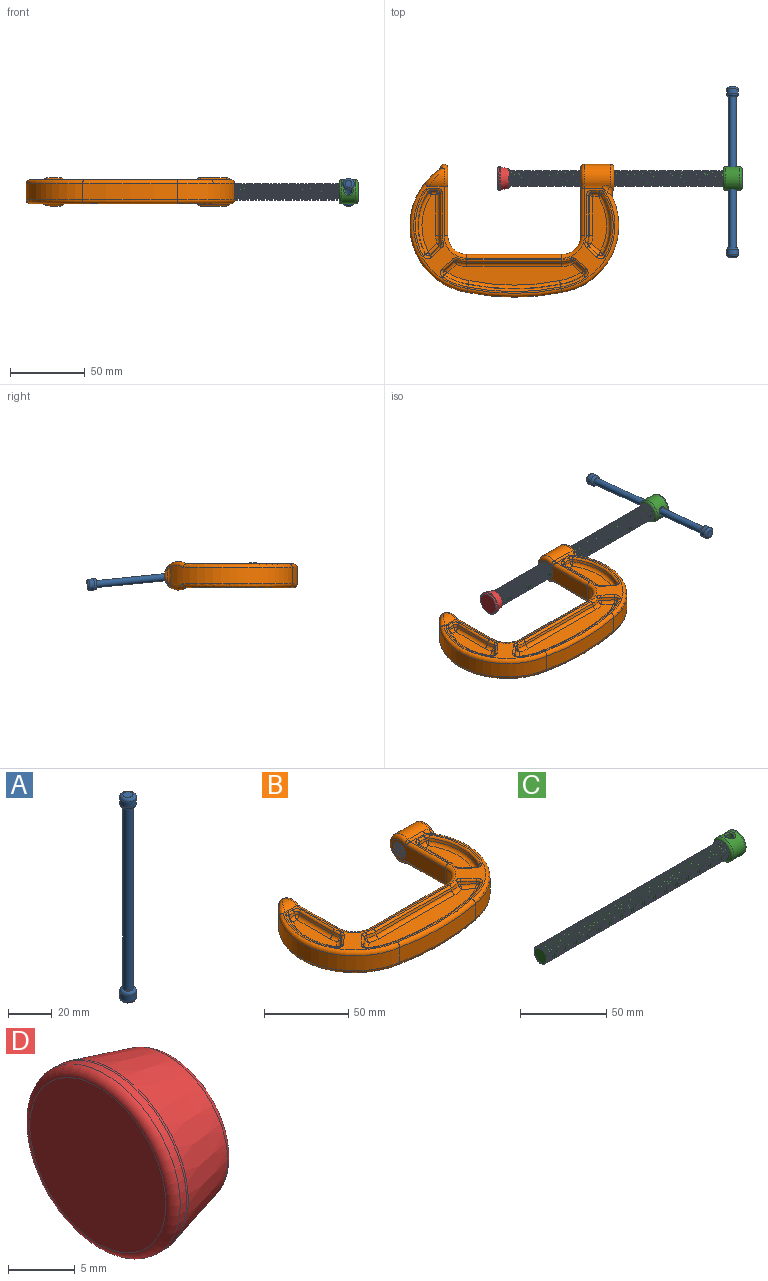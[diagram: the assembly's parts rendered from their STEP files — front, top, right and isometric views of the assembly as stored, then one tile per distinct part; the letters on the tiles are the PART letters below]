
ASSEMBLY  parts=4 mates=4
PART A: 11 faces, bbox 8.2x8.2x114.3 mm
  f0: cylinder r=2.37mm len=101.6mm, axis (0,0,-1), area 1516.1mm2, adj f1,f2
  f1: plane 4.75x4.75mm, normal (0,0,1), area 1.3mm2, adj f0,f9
  f2: plane 4.75x4.75mm, normal (0,0,-1), area 1.3mm2, adj f0,f5
  f3: cylinder r=3.81mm len=7.62mm, axis (0,0,1), area 79mm2, adj f5,f6
  f4: plane 4.57x4.57mm, normal (0,0,-1), area 16.4mm2, adj f6
  f5: torus R=2.29mm, axis (0,0,-1), area 49mm2, adj f2,f3
  f6: torus R=2.29mm, axis (0,0,-1), area 49mm2, adj f3,f4
  f7: cylinder r=3.81mm len=7.62mm, axis (0,0,-1), area 79mm2, adj f9,f10
  f8: plane 4.57x4.57mm, normal (0,0,1), area 16.4mm2, adj f10
  f9: torus R=2.29mm, axis (0,0,1), area 49mm2, adj f1,f7
  f10: torus R=2.29mm, axis (0,0,1), area 49mm2, adj f7,f8
PART B: 240 faces, bbox 147.4x103.1x20.9 mm
  f0: plane 45.3x14.18mm, normal (-1,0,0), area 415mm2, adj f8,f12,f13,f128,f236,f237,f238,f239
  f1: plane 14.21x14.21mm, normal (1,0,0), area 70.7mm2, adj f23,f24,f236,f237,f238,f239
  f2: cylinder r=9.53mm len=11.89mm, axis (1,0,0), area 65.6mm2, adj f10,f18,f19
  f3: cylinder r=45.26mm len=82.03mm, axis (0,0,-1), area 1160.1mm2, adj f6,f19,f20,f32,f133,f134
  f4: cylinder r=12.7mm len=12.7mm, axis (0,0,-1), area 215.4mm2, adj f5,f9,f16,f131
  f5: plane 45.09x13.97mm, normal (1,0,0), area 497.5mm2, adj f4,f17,f18,f132
  f6: cylinder r=160.34mm len=63.5mm, axis (0,0,-1), area 690mm2, adj f3,f7,f22,f136
  f7: cylinder r=45.26mm len=63.81mm, axis (0,0,-1), area 898.1mm2, adj f6,f21,f29,f30,f135,f141
  f8: cylinder r=12.7mm len=12.7mm, axis (0,0,-1), area 215.4mm2, adj f0,f9,f14,f129
  f9: plane 63.5x10.8mm, normal (0,1,0), area 685.5mm2, adj f4,f8,f15,f130
  f10: plane 134.76x72.01mm, normal (0,0,1), area 839.3mm2, adj f2,f13,f14,f15,f16,f17,f19,f20
  f11: cylinder r=9.53mm len=19.05mm, axis (-1,0,0), area 671.5mm2, adj f12,f23,f26,f27,f138,f139
  f12: torus R=6.99mm, axis (-1,0,0), area 147.2mm2, adj f0,f11,f25,f137
  f13: cylinder r=2.54mm len=33.67mm, axis (0,1,0), area 130mm2, adj f0,f10,f14,f25
  f14: torus R=15.24mm, axis (0,0,1), area 85.4mm2, adj f8,f10,f13,f15
  f15: cylinder r=2.54mm len=63.5mm, axis (1,0,0), area 253.4mm2, adj f9,f10,f14,f16
  f16: torus R=15.24mm, axis (0,0,1), area 85.4mm2, adj f4,f10,f15,f17
  f17: cylinder r=2.54mm len=33.67mm, axis (0,-1,0), area 132.7mm2, adj f5,f10,f16,f18
  f18: torus R=6.99mm, axis (-1,0,0), area 185.7mm2, adj f2,f5,f17,f31,f32,f126,f132,f142
  f19: bspline ~14.84x14.22mm, area 58.9mm2, adj f2,f3,f10,f20,f31
  f20: torus R=42.72mm, axis (0,0,1), area 369.9mm2, adj f3,f10,f19,f22
  f21: torus R=42.72mm, axis (0,0,1), area 340.5mm2, adj f7,f10,f22,f27,f28
  f22: torus R=157.8mm, axis (0,0,1), area 253.8mm2, adj f6,f10,f20,f21
  f23: torus R=6.99mm, axis (-1,0,0), area 177.3mm2, adj f1,f11,f24,f28,f29,f140,f141
  f24: bspline ~4.38x2.8mm, area 1.6mm2, adj f1,f23,f30
  f25: bspline ~3.1x3.02mm, area 4mm2, adj f12,f13,f26
  f26: cylinder r=5.08mm len=12.32mm, axis (-1,0,0), area 29.4mm2, adj f10,f11,f25,f27
  f27: bspline ~6.24x5.06mm, area 14.2mm2, adj f11,f21,f26,f28
  f28: bspline ~8.05x5.04mm, area 22.7mm2, adj f21,f23,f27,f29
  f29: bspline ~10x6.13mm, area 20.5mm2, adj f7,f23,f28,f30
  f30: bspline ~4.94x4.9mm, area 7mm2, adj f7,f24,f29,f141
  f31: bspline ~3.25x2.6mm, area 2.6mm2, adj f18,f19,f32
  f32: bspline ~12.33x2.68mm, area 31.2mm2, adj f3,f18,f31,f142
  f33: cone r=2.54mm half-angle=15deg, axis (0,0,1), area 4mm2, adj f34,f41,f74,f100
  f34: cone r=17.53mm half-angle=15deg, axis (0,0,-1), area 9.3mm2, adj f33,f35,f73,f102
  f35: plane 28.01x1.74mm, normal (-0.97,0,0.26), area 50.4mm2, adj f34,f36,f71,f104
  f36: cone r=2.54mm half-angle=15deg, axis (0,0,1), area 5.7mm2, adj f35,f37,f69,f103
  f37: plane 4.03x1.74mm, normal (0,-0.97,0.26), area 7.3mm2, adj f36,f38,f67,f101
  f38: cone r=2.54mm half-angle=15deg, axis (0,0,1), area 3.5mm2, adj f37,f39,f66,f99
  f39: cone r=40.43mm half-angle=15deg, axis (0,0,1), area 79.5mm2, adj f38,f40,f68,f97
  f40: cone r=2.54mm half-angle=15deg, axis (0,0,1), area 6.5mm2, adj f39,f41,f70,f96
  f41: plane 7.02x6.52mm, normal (-0.65,0.71,0.26), area 16.4mm2, adj f33,f40,f72,f98
  f42: plane 38.05x10.03mm, normal (0,0,1), area 277.8mm2, adj f67,f68,f71,f72,f73
  f43: plane 7.02x6.52mm, normal (0.65,-0.71,0.26), area 16.4mm2, adj f44,f54,f83,f123
  f44: cone r=2.54mm half-angle=15deg, axis (0,0,1), area 6.5mm2, adj f43,f45,f81,f125
  f45: cone r=40.43mm half-angle=15deg, axis (0,0,1), area 31.1mm2, adj f44,f46,f79,f124
  f46: cone r=155.51mm half-angle=15deg, axis (0,0,1), area 111.5mm2, adj f45,f47,f77,f122
  f47: cone r=40.43mm half-angle=15deg, axis (0,0,1), area 31.1mm2, adj f46,f48,f75,f120
  f48: cone r=2.54mm half-angle=15deg, axis (0,0,1), area 6.5mm2, adj f47,f49,f76,f118
  f49: plane 7.02x6.52mm, normal (-0.65,-0.71,0.26), area 16.4mm2, adj f48,f50,f78,f116
  f50: cone r=2.54mm half-angle=15deg, axis (0,0,1), area 4mm2, adj f49,f51,f80,f114
  f51: cone r=17.53mm half-angle=15deg, axis (0,0,-1), area 12mm2, adj f50,f52,f82,f115
  f52: plane 63.5x1.74mm, normal (0,-0.97,0.26), area 114.2mm2, adj f51,f53,f84,f117
  f53: cone r=17.53mm half-angle=15deg, axis (0,0,-1), area 12mm2, adj f52,f54,f86,f119
  f54: cone r=2.54mm half-angle=15deg, axis (0,0,1), area 4mm2, adj f43,f53,f85,f121
  f55: plane 89.13x13.72mm, normal (0,0,1), area 893.1mm2, adj f75,f77,f78,f79,f82,f83,f84,f86
  f56: plane 4.92x1.74mm, normal (0,-0.97,0.26), area 8.8mm2, adj f57,f64,f93,f110
  f57: cone r=2.54mm half-angle=15deg, axis (0,0,1), area 5.7mm2, adj f56,f58,f95,f108
  f58: plane 26.65x1.74mm, normal (0.97,0,0.26), area 47.9mm2, adj f57,f59,f94,f106
  f59: cone r=17.53mm half-angle=15deg, axis (0,0,-1), area 9.3mm2, adj f58,f60,f92,f105
  f60: cone r=2.54mm half-angle=15deg, axis (0,0,1), area 4mm2, adj f59,f61,f90,f107
  f61: plane 7.02x6.52mm, normal (0.65,0.71,0.26), area 16.4mm2, adj f60,f62,f88,f109
  f62: cone r=2.54mm half-angle=15deg, axis (0,0,1), area 6.5mm2, adj f61,f63,f87,f111
  f63: cone r=40.43mm half-angle=15deg, axis (0,0,1), area 76.5mm2, adj f62,f64,f89,f113
  f64: cone r=2.54mm half-angle=15deg, axis (0,0,1), area 3.7mm2, adj f56,f63,f91,f112
  f65: plane 36.69x10.03mm, normal (0,0,1), area 273.1mm2, adj f88,f89,f92,f93,f94
  f66: bspline ~2.45x1.88mm, area 2.1mm2, adj f38,f67,f68
  f67: cylinder r=2.54mm len=4.03mm, axis (-1,0,0), area 11.7mm2, adj f37,f42,f66,f69
  f68: torus R=37.21mm, axis (0,0,1), area 140.3mm2, adj f39,f42,f66,f70
  f69: bspline ~2.45x2.45mm, area 3.4mm2, adj f36,f67,f71
  f70: bspline ~2.8x2.75mm, area 3.9mm2, adj f40,f68,f72
  f71: cylinder r=2.54mm len=28.01mm, axis (0,1,0), area 92mm2, adj f35,f42,f69,f73
  f72: cylinder r=2.54mm len=8.37mm, axis (-0.74,-0.68,0), area 28.2mm2, adj f41,f42,f70,f74
  f73: torus R=20.75mm, axis (0,0,1), area 17.6mm2, adj f34,f42,f71,f74
  f74: bspline ~2.53x1.88mm, area 2.4mm2, adj f33,f72,f73
  f75: torus R=37.21mm, axis (0,0,1), area 54.4mm2, adj f47,f55,f76,f77
  f76: bspline ~2.81x2.78mm, area 3.9mm2, adj f48,f75,f78
  f77: torus R=152.29mm, axis (0,0,1), area 204.7mm2, adj f46,f55,f75,f79
  f78: cylinder r=2.54mm len=8.37mm, axis (0.74,-0.68,0), area 28.2mm2, adj f49,f55,f76,f80
  f79: torus R=37.21mm, axis (0,0,1), area 54.4mm2, adj f45,f55,f77,f81
  f80: bspline ~2.55x1.88mm, area 2.4mm2, adj f50,f78,f82
  f81: bspline ~2.81x2.78mm, area 3.9mm2, adj f44,f79,f83
  f82: torus R=20.75mm, axis (0,0,1), area 22.9mm2, adj f51,f55,f80,f84
  f83: cylinder r=2.54mm len=8.37mm, axis (-0.74,-0.68,0), area 28.2mm2, adj f43,f55,f81,f85
  f84: cylinder r=2.54mm len=63.5mm, axis (-1,0,0), area 211.1mm2, adj f52,f55,f82,f86
  f85: bspline ~2.55x1.88mm, area 2.4mm2, adj f54,f83,f86
  f86: torus R=20.75mm, axis (0,0,1), area 22.9mm2, adj f53,f55,f84,f85
  f87: bspline ~2.8x2.75mm, area 3.9mm2, adj f62,f88,f89
  f88: cylinder r=2.54mm len=8.37mm, axis (0.74,-0.68,0), area 28.2mm2, adj f61,f65,f87,f90
  f89: torus R=37.21mm, axis (0,0,1), area 134.8mm2, adj f63,f65,f87,f91
  f90: bspline ~2.53x1.88mm, area 2.4mm2, adj f60,f88,f92
  f91: bspline ~2.45x1.88mm, area 2.2mm2, adj f64,f89,f93
  f92: torus R=20.75mm, axis (0,0,1), area 17.6mm2, adj f59,f65,f90,f94
  f93: cylinder r=2.54mm len=4.92mm, axis (-1,0,0), area 14.6mm2, adj f56,f65,f91,f95
  f94: cylinder r=2.54mm len=26.65mm, axis (0,-1,0), area 87.5mm2, adj f58,f65,f92,f95
  f95: bspline ~2.45x2.45mm, area 3.4mm2, adj f57,f93,f94
  f96: torus R=3.71mm, axis (0,0,1), area 10.3mm2, adj f10,f40,f97,f98
  f97: torus R=41.6mm, axis (0,0,1), area 90mm2, adj f10,f39,f96,f99
  f98: cylinder r=1.52mm len=7.71mm, axis (0.74,0.68,0), area 18.2mm2, adj f10,f41,f96,f100
  f99: torus R=3.71mm, axis (0,0,1), area 5.5mm2, adj f10,f38,f97,f101
  f100: torus R=3.71mm, axis (0,0,1), area 6.3mm2, adj f10,f33,f98,f102
  f101: cylinder r=1.52mm len=4.03mm, axis (1,0,0), area 8mm2, adj f10,f37,f99,f103
  f102: torus R=16.36mm, axis (0,0,1), area 9.8mm2, adj f10,f34,f100,f104
  f103: torus R=3.71mm, axis (0,0,1), area 8.9mm2, adj f10,f36,f101,f104
  f104: cylinder r=1.52mm len=28.01mm, axis (0,-1,0), area 55.9mm2, adj f10,f35,f102,f103
  f105: torus R=16.36mm, axis (0,0,1), area 9.8mm2, adj f10,f59,f106,f107
  f106: cylinder r=1.52mm len=26.65mm, axis (0,1,0), area 53.2mm2, adj f10,f58,f105,f108
  f107: torus R=3.71mm, axis (0,0,1), area 6.3mm2, adj f10,f60,f105,f109
  f108: torus R=3.71mm, axis (0,0,1), area 8.9mm2, adj f10,f57,f106,f110
  f109: cylinder r=1.52mm len=7.71mm, axis (-0.74,0.68,0), area 18.2mm2, adj f10,f61,f107,f111
  f110: cylinder r=1.52mm len=4.92mm, axis (1,0,0), area 9.8mm2, adj f10,f56,f108,f112
  f111: torus R=3.71mm, axis (0,0,1), area 10.3mm2, adj f10,f62,f109,f113
  f112: torus R=3.71mm, axis (0,0,1), area 5.8mm2, adj f10,f64,f110,f113
  f113: torus R=41.6mm, axis (0,0,1), area 86.6mm2, adj f10,f63,f111,f112
  f114: torus R=3.71mm, axis (0,0,1), area 6.3mm2, adj f10,f50,f115,f116
  f115: torus R=16.36mm, axis (0,0,1), area 12.6mm2, adj f10,f51,f114,f117
  f116: cylinder r=1.52mm len=7.71mm, axis (-0.74,0.68,0), area 18.2mm2, adj f10,f49,f114,f118
  f117: cylinder r=1.52mm len=63.5mm, axis (1,0,0), area 126.7mm2, adj f10,f52,f115,f119
  f118: torus R=3.71mm, axis (0,0,1), area 10.3mm2, adj f10,f48,f116,f120
  f119: torus R=16.36mm, axis (0,0,1), area 12.6mm2, adj f10,f53,f117,f121
  f120: torus R=41.6mm, axis (0,0,1), area 35.2mm2, adj f10,f47,f118,f122
  f121: torus R=3.71mm, axis (0,0,1), area 6.3mm2, adj f10,f54,f119,f123
  f122: torus R=156.68mm, axis (0,0,1), area 124.3mm2, adj f10,f46,f120,f124
  f123: cylinder r=1.52mm len=7.71mm, axis (0.74,0.68,0), area 18.2mm2, adj f10,f43,f121,f125
  f124: torus R=41.6mm, axis (0,0,1), area 35.2mm2, adj f10,f45,f122,f125
  f125: torus R=3.71mm, axis (0,0,1), area 10.3mm2, adj f10,f44,f123,f124
  f126: cylinder r=9.53mm len=11.89mm, axis (1,0,0), area 65.6mm2, adj f18,f127,f133
  f127: plane 134.76x72.01mm, normal (0,0,-1), area 839.3mm2, adj f126,f128,f129,f130,f131,f132,f133,f134
  f128: cylinder r=2.54mm len=33.67mm, axis (0,1,0), area 130mm2, adj f0,f127,f129,f137
  f129: torus R=15.24mm, axis (0,0,-1), area 85.4mm2, adj f8,f127,f128,f130
  f130: cylinder r=2.54mm len=63.5mm, axis (1,0,0), area 253.4mm2, adj f9,f127,f129,f131
  f131: torus R=15.24mm, axis (0,0,-1), area 85.4mm2, adj f4,f127,f130,f132
  f132: cylinder r=2.54mm len=33.67mm, axis (0,-1,0), area 132.7mm2, adj f5,f18,f127,f131
  f133: bspline ~14.84x14.22mm, area 58.9mm2, adj f3,f126,f127,f134,f142
  f134: torus R=42.72mm, axis (0,0,-1), area 369.9mm2, adj f3,f127,f133,f136
  f135: torus R=42.72mm, axis (0,0,-1), area 340.5mm2, adj f7,f127,f136,f139,f140
  f136: torus R=157.8mm, axis (0,0,-1), area 253.8mm2, adj f6,f127,f134,f135
  f137: bspline ~3.1x3.02mm, area 4mm2, adj f12,f128,f138
  f138: cylinder r=5.08mm len=12.32mm, axis (-1,0,0), area 29.4mm2, adj f11,f127,f137,f139
  f139: bspline ~6.24x5.06mm, area 14.2mm2, adj f11,f135,f138,f140
  f140: bspline ~8.05x5.04mm, area 22.7mm2, adj f23,f135,f139,f141
  f141: bspline ~8.1x6.12mm, area 20.5mm2, adj f7,f23,f30,f140
  f142: bspline ~3.17x2.51mm, area 2.6mm2, adj f18,f32,f133
  f143: cone r=2.54mm half-angle=15deg, axis (0,0,-1), area 4mm2, adj f144,f151,f184,f210
  f144: cone r=17.53mm half-angle=15deg, axis (0,0,1), area 9.3mm2, adj f143,f145,f183,f212
  f145: plane 28.01x1.74mm, normal (-0.97,0,-0.26), area 50.4mm2, adj f144,f146,f181,f214
  f146: cone r=2.54mm half-angle=15deg, axis (0,0,-1), area 5.7mm2, adj f145,f147,f179,f213
  f147: plane 4.03x1.74mm, normal (0,-0.97,-0.26), area 7.3mm2, adj f146,f148,f177,f211
  f148: cone r=2.54mm half-angle=15deg, axis (0,0,-1), area 3.5mm2, adj f147,f149,f176,f209
  f149: cone r=40.43mm half-angle=15deg, axis (0,0,-1), area 79.5mm2, adj f148,f150,f178,f207
  f150: cone r=2.54mm half-angle=15deg, axis (0,0,-1), area 6.5mm2, adj f149,f151,f180,f206
  f151: plane 7.02x6.52mm, normal (-0.65,0.71,-0.26), area 16.4mm2, adj f143,f150,f182,f208
  f152: plane 38.05x10.03mm, normal (0,0,-1), area 277.8mm2, adj f177,f178,f181,f182,f183
  f153: plane 7.02x6.52mm, normal (0.65,-0.71,-0.26), area 16.4mm2, adj f154,f164,f193,f233
  f154: cone r=2.54mm half-angle=15deg, axis (0,0,-1), area 6.5mm2, adj f153,f155,f191,f235
  f155: cone r=40.43mm half-angle=15deg, axis (0,0,-1), area 31.1mm2, adj f154,f156,f189,f234
  f156: cone r=155.51mm half-angle=15deg, axis (0,0,-1), area 111.5mm2, adj f155,f157,f187,f232
  f157: cone r=40.43mm half-angle=15deg, axis (0,0,-1), area 31.1mm2, adj f156,f158,f185,f230
  f158: cone r=2.54mm half-angle=15deg, axis (0,0,-1), area 6.5mm2, adj f157,f159,f186,f228
  f159: plane 7.02x6.52mm, normal (-0.65,-0.71,-0.26), area 16.4mm2, adj f158,f160,f188,f226
  f160: cone r=2.54mm half-angle=15deg, axis (0,0,-1), area 4mm2, adj f159,f161,f190,f224
  f161: cone r=17.53mm half-angle=15deg, axis (0,0,1), area 12mm2, adj f160,f162,f192,f225
  f162: plane 63.5x1.74mm, normal (0,-0.97,-0.26), area 114.2mm2, adj f161,f163,f194,f227
  f163: cone r=17.53mm half-angle=15deg, axis (0,0,1), area 12mm2, adj f162,f164,f196,f229
  f164: cone r=2.54mm half-angle=15deg, axis (0,0,-1), area 4mm2, adj f153,f163,f195,f231
  f165: plane 89.13x13.72mm, normal (0,0,-1), area 893.1mm2, adj f185,f187,f188,f189,f192,f193,f194,f196
  f166: plane 4.92x1.74mm, normal (0,-0.97,-0.26), area 8.8mm2, adj f167,f174,f203,f220
  f167: cone r=2.54mm half-angle=15deg, axis (0,0,-1), area 5.7mm2, adj f166,f168,f205,f218
  f168: plane 26.65x1.74mm, normal (0.97,0,-0.26), area 47.9mm2, adj f167,f169,f204,f216
  f169: cone r=17.53mm half-angle=15deg, axis (0,0,1), area 9.3mm2, adj f168,f170,f202,f215
  f170: cone r=2.54mm half-angle=15deg, axis (0,0,-1), area 4mm2, adj f169,f171,f200,f217
  f171: plane 7.02x6.52mm, normal (0.65,0.71,-0.26), area 16.4mm2, adj f170,f172,f198,f219
  f172: cone r=2.54mm half-angle=15deg, axis (0,0,-1), area 6.5mm2, adj f171,f173,f197,f221
  f173: cone r=40.43mm half-angle=15deg, axis (0,0,-1), area 76.5mm2, adj f172,f174,f199,f223
  f174: cone r=2.54mm half-angle=15deg, axis (0,0,-1), area 3.7mm2, adj f166,f173,f201,f222
  f175: plane 36.69x10.03mm, normal (0,0,-1), area 273.1mm2, adj f198,f199,f202,f203,f204
  f176: bspline ~2.45x1.88mm, area 2.1mm2, adj f148,f177,f178
  f177: cylinder r=2.54mm len=4.03mm, axis (-1,0,0), area 11.7mm2, adj f147,f152,f176,f179
  f178: torus R=37.21mm, axis (0,0,-1), area 140.3mm2, adj f149,f152,f176,f180
  f179: bspline ~2.45x2.45mm, area 3.4mm2, adj f146,f177,f181
  f180: bspline ~2.8x2.75mm, area 3.9mm2, adj f150,f178,f182
  f181: cylinder r=2.54mm len=28.01mm, axis (0,1,0), area 92mm2, adj f145,f152,f179,f183
  f182: cylinder r=2.54mm len=8.37mm, axis (-0.74,-0.68,0), area 28.2mm2, adj f151,f152,f180,f184
  f183: torus R=20.75mm, axis (0,0,-1), area 17.6mm2, adj f144,f152,f181,f184
  f184: bspline ~2.53x1.88mm, area 2.4mm2, adj f143,f182,f183
  f185: torus R=37.21mm, axis (0,0,-1), area 54.4mm2, adj f157,f165,f186,f187
  f186: bspline ~2.81x2.78mm, area 3.9mm2, adj f158,f185,f188
  f187: torus R=152.29mm, axis (0,0,-1), area 204.7mm2, adj f156,f165,f185,f189
  f188: cylinder r=2.54mm len=8.37mm, axis (0.74,-0.68,0), area 28.2mm2, adj f159,f165,f186,f190
  f189: torus R=37.21mm, axis (0,0,-1), area 54.4mm2, adj f155,f165,f187,f191
  f190: bspline ~2.55x1.88mm, area 2.4mm2, adj f160,f188,f192
  f191: bspline ~2.81x2.78mm, area 3.9mm2, adj f154,f189,f193
  f192: torus R=20.75mm, axis (0,0,-1), area 22.9mm2, adj f161,f165,f190,f194
  f193: cylinder r=2.54mm len=8.37mm, axis (-0.74,-0.68,0), area 28.2mm2, adj f153,f165,f191,f195
  f194: cylinder r=2.54mm len=63.5mm, axis (-1,0,0), area 211.1mm2, adj f162,f165,f192,f196
  f195: bspline ~2.55x1.88mm, area 2.4mm2, adj f164,f193,f196
  f196: torus R=20.75mm, axis (0,0,-1), area 22.9mm2, adj f163,f165,f194,f195
  f197: bspline ~2.8x2.75mm, area 3.9mm2, adj f172,f198,f199
  f198: cylinder r=2.54mm len=8.37mm, axis (0.74,-0.68,0), area 28.2mm2, adj f171,f175,f197,f200
  f199: torus R=37.21mm, axis (0,0,-1), area 134.8mm2, adj f173,f175,f197,f201
  f200: bspline ~2.53x1.88mm, area 2.4mm2, adj f170,f198,f202
  f201: bspline ~2.45x1.88mm, area 2.2mm2, adj f174,f199,f203
  f202: torus R=20.75mm, axis (0,0,-1), area 17.6mm2, adj f169,f175,f200,f204
  f203: cylinder r=2.54mm len=4.92mm, axis (-1,0,0), area 14.6mm2, adj f166,f175,f201,f205
  f204: cylinder r=2.54mm len=26.65mm, axis (0,-1,0), area 87.5mm2, adj f168,f175,f202,f205
  f205: bspline ~2.45x2.45mm, area 3.4mm2, adj f167,f203,f204
  f206: torus R=3.71mm, axis (0,0,-1), area 10.3mm2, adj f127,f150,f207,f208
  f207: torus R=41.6mm, axis (0,0,-1), area 90mm2, adj f127,f149,f206,f209
  f208: cylinder r=1.52mm len=7.71mm, axis (0.74,0.68,0), area 18.2mm2, adj f127,f151,f206,f210
  f209: torus R=3.71mm, axis (0,0,-1), area 5.5mm2, adj f127,f148,f207,f211
  f210: torus R=3.71mm, axis (0,0,-1), area 6.3mm2, adj f127,f143,f208,f212
  f211: cylinder r=1.52mm len=4.03mm, axis (1,0,0), area 8mm2, adj f127,f147,f209,f213
  f212: torus R=16.36mm, axis (0,0,-1), area 9.8mm2, adj f127,f144,f210,f214
  f213: torus R=3.71mm, axis (0,0,-1), area 8.9mm2, adj f127,f146,f211,f214
  f214: cylinder r=1.52mm len=28.01mm, axis (0,-1,0), area 55.9mm2, adj f127,f145,f212,f213
  f215: torus R=16.36mm, axis (0,0,-1), area 9.8mm2, adj f127,f169,f216,f217
  f216: cylinder r=1.52mm len=26.65mm, axis (0,1,0), area 53.2mm2, adj f127,f168,f215,f218
  f217: torus R=3.71mm, axis (0,0,-1), area 6.3mm2, adj f127,f170,f215,f219
  f218: torus R=3.71mm, axis (0,0,-1), area 8.9mm2, adj f127,f167,f216,f220
  f219: cylinder r=1.52mm len=7.71mm, axis (-0.74,0.68,0), area 18.2mm2, adj f127,f171,f217,f221
  f220: cylinder r=1.52mm len=4.92mm, axis (1,0,0), area 9.8mm2, adj f127,f166,f218,f222
  f221: torus R=3.71mm, axis (0,0,-1), area 10.3mm2, adj f127,f172,f219,f223
  f222: torus R=3.71mm, axis (0,0,-1), area 5.8mm2, adj f127,f174,f220,f223
  f223: torus R=41.6mm, axis (0,0,-1), area 86.6mm2, adj f127,f173,f221,f222
  f224: torus R=3.71mm, axis (0,0,-1), area 6.3mm2, adj f127,f160,f225,f226
  f225: torus R=16.36mm, axis (0,0,-1), area 12.6mm2, adj f127,f161,f224,f227
  f226: cylinder r=1.52mm len=7.71mm, axis (-0.74,0.68,0), area 18.2mm2, adj f127,f159,f224,f228
  f227: cylinder r=1.52mm len=63.5mm, axis (1,0,0), area 126.7mm2, adj f127,f162,f225,f229
  f228: torus R=3.71mm, axis (0,0,-1), area 10.3mm2, adj f127,f158,f226,f230
  f229: torus R=16.36mm, axis (0,0,-1), area 12.6mm2, adj f127,f163,f227,f231
  f230: torus R=41.6mm, axis (0,0,-1), area 35.2mm2, adj f127,f157,f228,f232
  f231: torus R=3.71mm, axis (0,0,-1), area 6.3mm2, adj f127,f164,f229,f233
  f232: torus R=156.68mm, axis (0,0,-1), area 124.3mm2, adj f127,f156,f230,f234
  f233: cylinder r=1.52mm len=7.71mm, axis (0.74,0.68,0), area 18.2mm2, adj f127,f153,f231,f235
  f234: torus R=41.6mm, axis (0,0,-1), area 35.2mm2, adj f127,f155,f232,f235
  f235: torus R=3.71mm, axis (0,0,-1), area 10.3mm2, adj f127,f154,f233,f234
  f236: cylinder r=5.56mm len=22.23mm, axis (-1,0,0), area 259.9mm2, adj f0,f1,f237,f238
  f237: bspline ~22.77x12.85mm, area 365.3mm2, adj f0,f1,f236,f239
  f238: bspline ~23.07x12.85mm, area 365.3mm2, adj f0,f1,f236,f239
  f239: cylinder r=4.67mm len=22.23mm, axis (-1,0,0), area 225.7mm2, adj f0,f1,f237,f238
PART C: 13 faces, bbox 162.5x17.4x17.4 mm
  f0: plane 13.07x13.07mm, normal (-1,0,0), area 46.6mm2, adj f3,f4,f5,f6,f9
  f1: cylinder r=7.94mm len=15.88mm, axis (1,0,0), area 411.2mm2, adj f8,f9,f11,f12
  f2: plane 10.67x10.46mm, normal (-1,0,0), area 82.6mm2, adj f3,f4,f5,f6
  f3: cylinder r=5.56mm len=149.23mm, axis (-1,0,0), area -309mm2, adj f0,f2,f4,f5
  f4: bspline ~149.91x12.85mm, area 2458.9mm2, adj f0,f2,f3,f6
  f5: bspline ~149.91x12.85mm, area 2458.1mm2, adj f0,f2,f3,f6
  f6: cylinder r=4.67mm len=149.23mm, axis (-1,0,0), area -750.6mm2, adj f0,f2,f4,f5
  f7: plane 12.83x12.83mm, normal (1,0,0), area 129.2mm2, adj f8
  f8: torus R=6.41mm, axis (1,0,0), area 111.1mm2, adj f1,f7
  f9: torus R=6.41mm, axis (1,0,0), area 111.1mm2, adj f0,f1
  f10: cylinder r=2.37mm len=14.35mm, axis (0,0,1), area 203.5mm2, adj f11,f12
  f11: bspline ~6.95x6.28mm, area 23.6mm2, adj f1,f10
  f12: bspline ~6.95x6.28mm, area 23.6mm2, adj f1,f10
PART D: 12 faces, bbox 8.6x17.4x17.4 mm
  f0: plane 11.56x11.56mm, normal (1,0,0), area 17.7mm2, adj f6,f7,f8,f9,f10
  f1: cone r=7.94mm half-angle=15deg, axis (-1,0,0), area 264.5mm2, adj f4,f6
  f2: plane 14.35x14.35mm, normal (-1,0,0), area 161.8mm2, adj f5
  f3: cylinder r=7.94mm len=15.88mm, axis (-1,0,0), area 33mm2, adj f4,f5
  f4: torus R=7.18mm, axis (1,0,0), area 9.9mm2, adj f1,f3
  f5: torus R=7.18mm, axis (-1,0,0), area 57.6mm2, adj f2,f3
  f6: torus R=5.65mm, axis (-1,0,0), area 38.1mm2, adj f0,f1
  f7: cylinder r=5.56mm len=11.13mm, axis (-1,0,0), area 80.5mm2, adj f0,f8,f9,f11
  f8: bspline ~12.85x11.13mm, area 104.1mm2, adj f0,f7,f10,f11
  f9: bspline ~12.85x11.13mm, area 104.2mm2, adj f0,f7,f10,f11
  f10: cylinder r=4.67mm len=9.35mm, axis (-1,0,0), area 71.4mm2, adj f0,f8,f9,f11
  f11: plane 10.67x10.46mm, normal (1,0,0), area 82.6mm2, adj f7,f8,f9,f10
PLACE A rot(axis=(0.87,0.33,-0.36),91.9deg) t=(-65.42,8.83,51.18)mm
PLACE B t=(-110.74,-26.2,-1.54)mm fixed
PLACE C rot(axis=(1,0,0),84.2deg) t=(-75.85,-3.36,-26.81)mm
PLACE D rot(axis=(1,0,0),90.4deg) t=(-75.85,-0.61,-26.94)mm
MATE cylindrical A.f0 <-> C.f10  axis (0,0.99,-0.1) through (35.28,3.46,-1.97)mm
MATE cylindrical D.f7 <-> C.f1  axis (1,0,0) through (-120.4,-0.8,-1.54)mm
MATE cylindrical C.f1 <-> B.f236  axis (1,0,0) through (40.1,-0.8,-1.54)mm
MATE planar D.f11 <-> C.f2  axis (1,0,0) through (-120.3,-0.72,-2.08)mm
